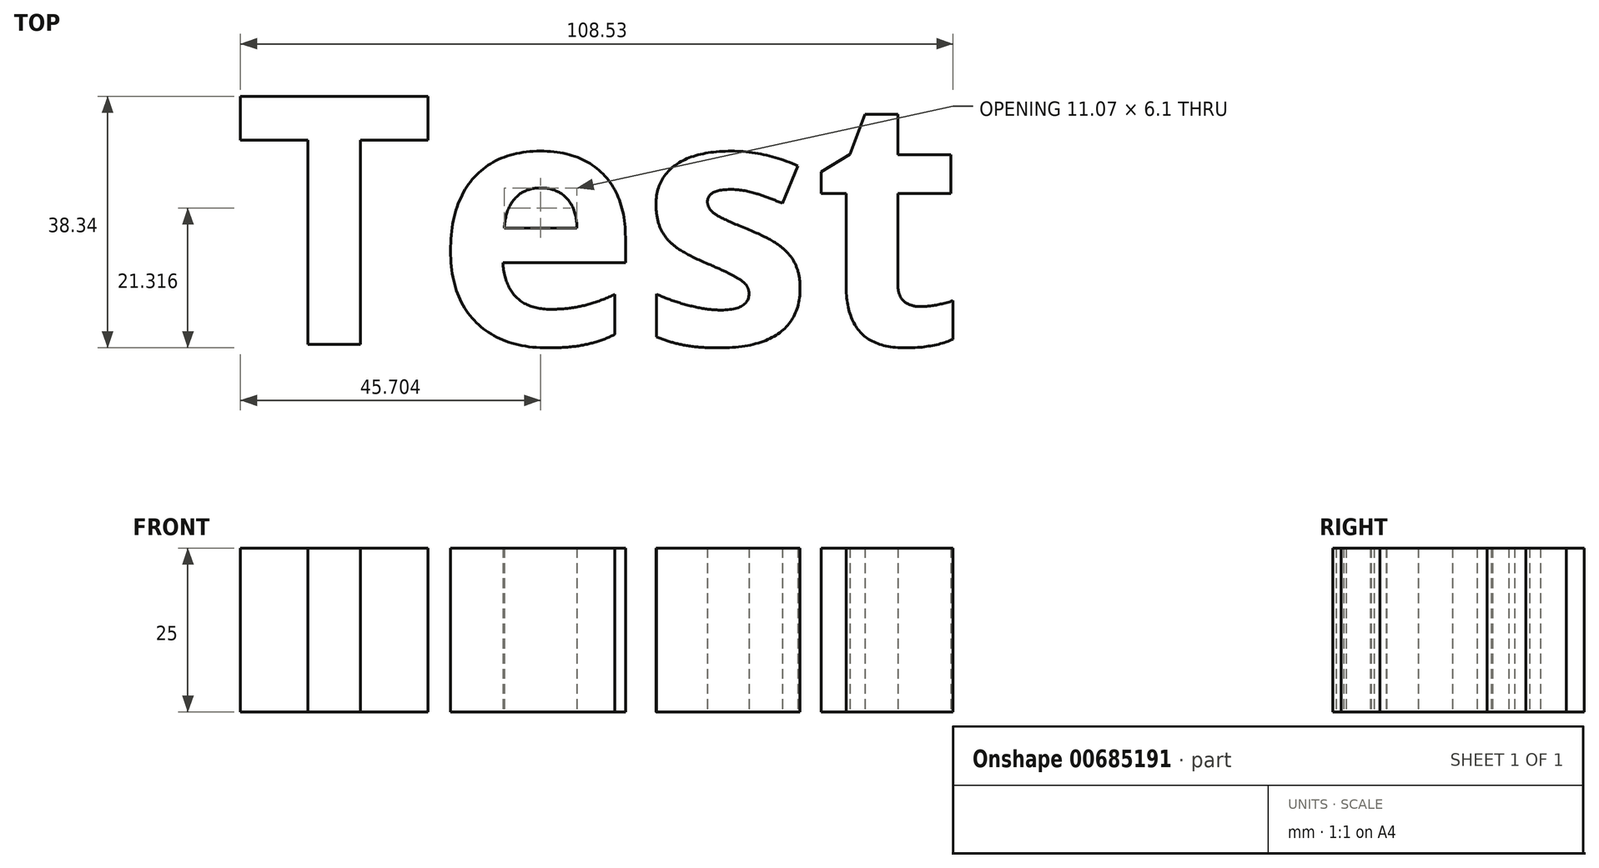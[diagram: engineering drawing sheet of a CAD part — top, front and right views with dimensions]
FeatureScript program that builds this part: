
annotation { "Feature Type Name" : "Feature", "Feature Type Description" : "" }
export const myFeature = defineFeature(function(context is Context, id is Id, definition is map)
    precondition{}
    {
        {
            var Q0;
            Q0=qCreatedBy(makeId("Top.planeOp"),FACE);
            var sketch = newSketch(context, id + "F0", { "sketchPlane" : qUnion([Q0])});
            skText(sketch, "E0", { "text": "Test", "fontName": "OpenSans-Bold.ttf"});
            const initialGuessF0  = {"E0": [0, -0.03814, 1, 0, 0.03814]};
            skSetInitialGuess(sketch, initialGuessF0);
            skSolve(sketch);
        }
        {
            var Q0;
            Q0=makeQuery(id+"F0.imprint","IMPRINT",FACE,{"disambiguationData":[TD([[makeQuery(id+"F0.imprint","IMPRINT",EDGE,{"derivedFrom":sQuery(id+"F0.wireOp",EDGE,"E0.sketch_text.stroke-0")}),-1.0]])]});
            var Q1;
            Q1=makeQuery(id+"F0.imprint","IMPRINT",FACE,{"disambiguationData":[TD([[makeQuery(id+"F0.imprint","IMPRINT",EDGE,{"derivedFrom":sQuery(id+"F0.wireOp",EDGE,"E0.sketch_text.stroke-8")}),-1.0]])]});
            var Q2;
            Q2=makeQuery(id+"F0.imprint","IMPRINT",FACE,{"disambiguationData":[TD([[makeQuery(id+"F0.imprint","IMPRINT",EDGE,{"derivedFrom":sQuery(id+"F0.wireOp",EDGE,"E0.sketch_text.stroke-28")}),-1.0]])]});
            var Q3;
            Q3=makeQuery(id+"F0.imprint","IMPRINT",FACE,{"disambiguationData":[TD([[makeQuery(id+"F0.imprint","IMPRINT",EDGE,{"derivedFrom":sQuery(id+"F0.wireOp",EDGE,"E0.sketch_text.stroke-54")}),-1.0]])]});
            extrude(context, id + "F1", {"entities" : qUnion([Q0, Q1, Q2, Q3]), "depth" : 25 * mm, "offsetDistance" : 25 * mm});
        }
    });
